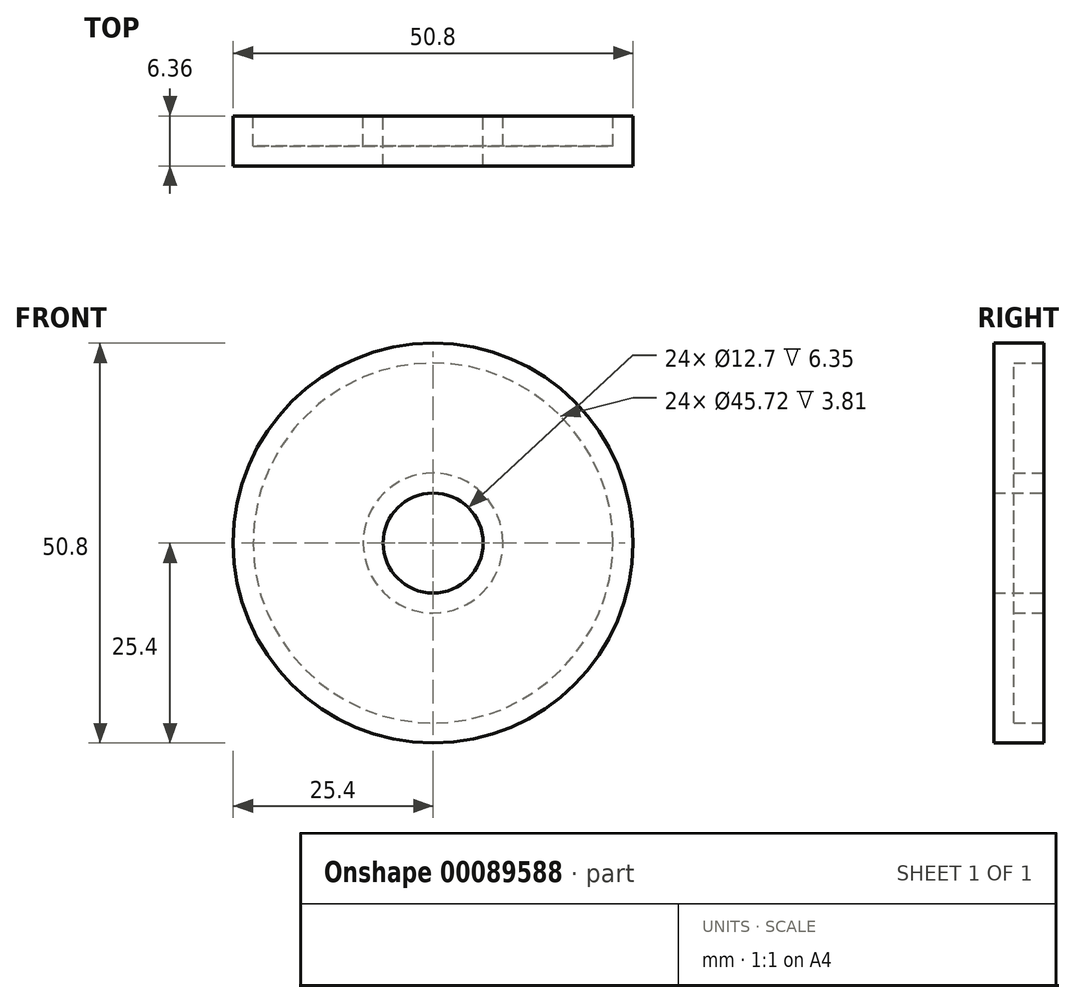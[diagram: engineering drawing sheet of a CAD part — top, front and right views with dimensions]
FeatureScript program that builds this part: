
annotation { "Feature Type Name" : "Feature", "Feature Type Description" : "" }
export const myFeature = defineFeature(function(context is Context, id is Id, definition is map)
    precondition{}
    {
        {
            var Q0;
            Q0=qCreatedBy(makeId("Front.planeOp"),FACE);
            var sketch = newSketch(context, id + "F0", { "sketchPlane" : qUnion([Q0])});
            skCircle(sketch, "E0", {"center": v(0, 0) * mm, "radius": 25.4 * mm});
            skCircle(sketch, "E1", {"center": v(0, 0) * mm, "radius": 6.35 * mm});
            skSolve(sketch);
        }
        {
            var Q0;
            Q0=qSketchRegion(id+"F0",true);
            extrude(context, id + "F1", {"entities" : qUnion([Q0]), "endBound" : BoundingType.SYMMETRIC, "depth" : 6.35 * mm});
        }
        {
            var Q0;
            Q0=makeQuery(id+"F1.opExtrude","CAP_FACE",FACE,{"disambiguationData":[OSD([sQuery(id+"F0.wireOp",EDGE,"E0"),sQuery(id+"F0.wireOp",EDGE,"E1")])],"isStart":true});
            shell(context, id + "F2", {"entities" : qUnion([Q0]), "thickness" : 2.54 * mm});
        }
    });
